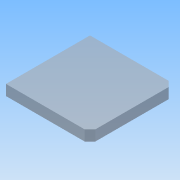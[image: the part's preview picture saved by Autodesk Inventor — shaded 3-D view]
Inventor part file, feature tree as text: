
AUTODESK INVENTOR PART (.ipt)
format: ipt  version: 2016 (Build 200138000, 138)  size: 69,632 bytes
history: native  units: mm
features: extrude x1, sketch x1
ambient origin geometry x8: Origin, YZ Plane, XZ Plane, XY Plane, X Axis, Y Axis, Z Axis, Center Point
bodies: Volumenkörper1 (feature_tree)
feature tree (2):
  extrude  "Extrusion1"  Depth=80.0mm
  sketch  "Skizze1"  dims[d0=90.0mm d1=80.0mm d2=10.0mm d3=0.0mm]
